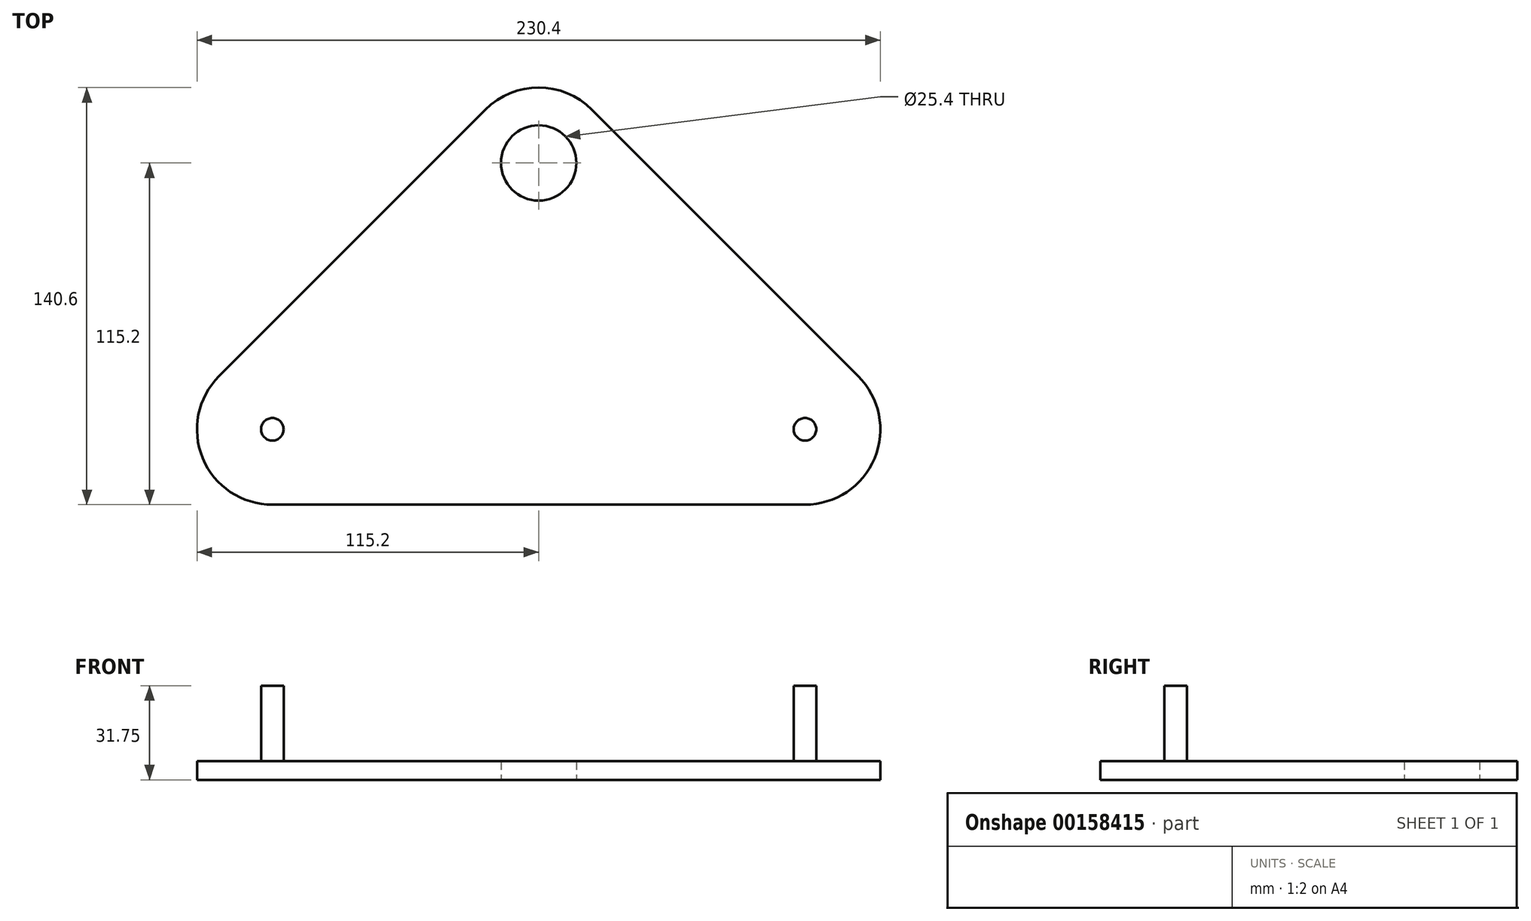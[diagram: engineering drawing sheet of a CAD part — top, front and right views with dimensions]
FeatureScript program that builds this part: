
annotation { "Feature Type Name" : "Feature", "Feature Type Description" : "" }
export const myFeature = defineFeature(function(context is Context, id is Id, definition is map)
    precondition{}
    {
        {
            var Q0;
            Q0=qCreatedBy(makeId("Top.planeOp"),FACE);
            var sketch = newSketch(context, id + "F0", { "sketchPlane" : qUnion([Q0])});
            skCircle(sketch, "E0", {"center": v(0, 0) * mm, "radius": 25.4 * mm});
            skLineSegment(sketch, "E1", {"start": v(0, 0) * mm, "end": v(-89.8, -89.8) * mm});
            skLineSegment(sketch, "E2", {"start": v(-89.8, -89.8) * mm, "end": v(89.8, -89.8) * mm});
            skLineSegment(sketch, "E3", {"start": v(89.8, -89.8) * mm, "end": v(0, 0) * mm});
            skCircle(sketch, "E4", {"center": v(-89.8, -89.8) * mm, "radius": 25.4 * mm});
            skCircle(sketch, "E5", {"center": v(89.8, -89.8) * mm, "radius": 25.4 * mm});
            skSolve(sketch);
        }
        {
            var Q0;
            Q0=qCreatedBy(makeId("Top.planeOp"),FACE);
            var sketch = newSketch(context, id + "F1", { "sketchPlane" : qUnion([Q0])});
            skLineSegment(sketch, "E6.0", {"start": v(107.76, -71.84) * mm, "end": v(17.96, 17.96) * mm});
            skLineSegment(sketch, "E6.1", {"start": v(-89.8, -115.2) * mm, "end": v(89.8, -115.2) * mm});
            skLineSegment(sketch, "E6.2", {"start": v(-17.96, 17.96) * mm, "end": v(-107.76, -71.84) * mm});
            skPoint(sketch, "E7.visualSharp", {"position": v(0, 35.92) * mm});
            skArc(sketch, "E7.filletArc", {"start": v(17.96, 17.96) * mm, "mid": v(0, 25.4) * mm, "end": v(-17.96, 17.96) * mm});
            skPoint(sketch, "E8.visualSharp", {"position": v(151.12, -115.2) * mm});
            skArc(sketch, "E8.filletArc", {"start": v(89.8, -115.2) * mm, "mid": v(113.27, -99.52) * mm, "end": v(107.76, -71.84) * mm});
            skPoint(sketch, "E9.visualSharp", {"position": v(-151.12, -115.2) * mm});
            skArc(sketch, "E9.filletArc", {"start": v(-107.76, -71.84) * mm, "mid": v(-113.27, -99.52) * mm, "end": v(-89.8, -115.2) * mm});
            skSolve(sketch);
        }
        {
            var Q0;
            Q0=makeQuery(id+"F1.imprint","IMPRINT",FACE,{"disambiguationData":[TD([[makeQuery(id+"F1.imprint","IMPRINT",EDGE,{"derivedFrom":sQuery(id+"F1.wireOp",EDGE,"E6.0")}),1.0]])]});
            extrude(context, id + "F2", {"entities" : qUnion([Q0]), "depth" : 6.35 * mm});
        }
        {
            var Q0;
            Q0=makeQuery(id+"F2.opExtrude","CAP_FACE",FACE,{"disambiguationData":[OSD([sQuery(id+"F1.wireOp",EDGE,"E6.0"),sQuery(id+"F1.wireOp",EDGE,"E6.1"),sQuery(id+"F1.wireOp",EDGE,"E6.2"),sQuery(id+"F1.wireOp",EDGE,"E7.filletArc"),sQuery(id+"F1.wireOp",EDGE,"E8.filletArc"),sQuery(id+"F1.wireOp",EDGE,"E9.filletArc")])],"isStart":false});
            var sketch = newSketch(context, id + "F3", { "sketchPlane" : qUnion([Q0])});
            skCircle(sketch, "E10", {"center": v(89.8, -89.8) * mm, "radius": 3.81 * mm});
            skCircle(sketch, "E11", {"center": v(-89.8, -89.8) * mm, "radius": 3.81 * mm});
            skCircle(sketch, "E12", {"center": v(0, 0) * mm, "radius": 3.81 * mm});
            skSolve(sketch);
        }
        {
            var Q0;
            Q0=makeQuery(id+"F3.imprint","IMPRINT",FACE,{"disambiguationData":[TD([[makeQuery(id+"F3.imprint","IMPRINT",EDGE,{"derivedFrom":sQuery(id+"F3.wireOp",EDGE,"E10")}),1.0]])]});
            var Q1;
            Q1=makeQuery(id+"F3.imprint","IMPRINT",FACE,{"disambiguationData":[TD([[makeQuery(id+"F3.imprint","IMPRINT",EDGE,{"derivedFrom":sQuery(id+"F3.wireOp",EDGE,"E11")}),1.0]])]});
            extrude(context, id + "F4", {"entities" : qUnion([Q0, Q1]), "operationType" : NewBodyOperationType.ADD, "depth" : 25.4 * mm});
        }
        {
            var Q0;
            Q0=sQuery(id+"F0.wireOp",VERTEX,"E0.center");
            var Q1;
            Q1=makeQuery(id+"F2.opExtrude","SWEPT_BODY",BODY,{"disambiguationData":[OSD([sQuery(id+"F1.wireOp",EDGE,"E6.0"),sQuery(id+"F1.wireOp",EDGE,"E6.1"),sQuery(id+"F1.wireOp",EDGE,"E6.2"),sQuery(id+"F1.wireOp",EDGE,"E7.filletArc"),sQuery(id+"F1.wireOp",EDGE,"E8.filletArc"),sQuery(id+"F1.wireOp",EDGE,"E9.filletArc")])]});
            hole(context, id + "F5", {"style" : HoleStyle.SIMPLE, "endStyle" : HoleEndStyle.THROUGH, "oppositeDirection" : true, "holeDiameter" : 25.4 * mm, "locations" : qUnion([Q0]), "scope" : qUnion([Q1]), "isTappedThrough" : true});
        }
    });
